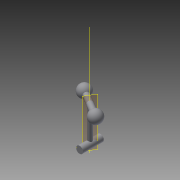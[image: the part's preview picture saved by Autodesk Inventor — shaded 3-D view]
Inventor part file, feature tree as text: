
AUTODESK INVENTOR PART (.ipt)
format: ipt  version: 2014 (Build 180170000, 170)  size: 128,512 bytes
history: native  units: mm
features: sketch x4, plane x2, extrude x2, revolve x2, mirror x1, other x1
ambient origin geometry x8: Origin, YZ Plane, XZ Plane, XY Plane, X Axis, Y Axis, Z Axis, Center Point
bodies: Solid1 (feature_tree)
feature tree (12):
  sketch  "Sketch1"  dims[d0=500.0mm d1=3000.0mm]
  plane  "Work Plane4"
  extrude  "Extrusion2"  Depth=3000.0mm
  revolve  "Revolution1"  [1 undecoded]
  plane  "Work Plane5"
  extrude  "Extrusion5"  Depth=10.297443mm
  revolve  "Revolution4"  Angle=90.0deg
  mirror  "Mirror5"
  sketch  "Sketch2"  dims[d4=600.0mm d5=5000.0mm d6=0.0mm]
  other  "Work Axis2"
  sketch  "Sketch8"  dims[d7=90.0deg d14=10.297443mm]
  sketch  "Sketch9"  dims[d19=2344.25mm d20=0.0mm d21=90.0deg]
note: 1 required parameter value undecoded (feature->parameter linkage not recoverable at this tier; creation-order binding heuristic only, values carry confidence <= 0.55)
